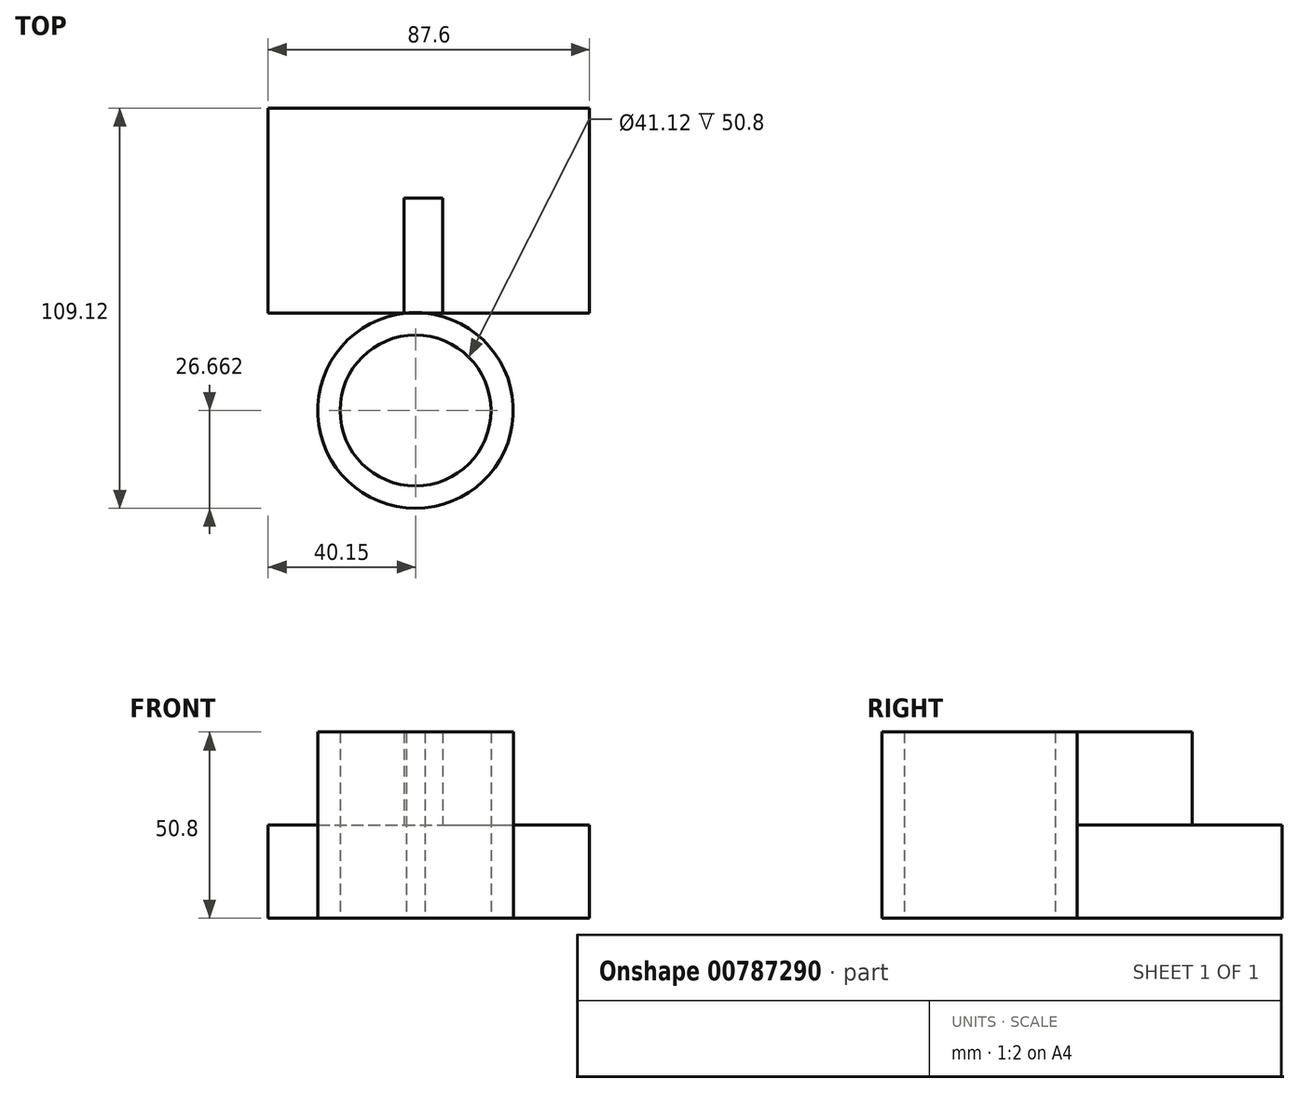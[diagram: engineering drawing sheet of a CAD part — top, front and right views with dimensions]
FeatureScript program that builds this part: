
annotation { "Feature Type Name" : "Feature", "Feature Type Description" : "" }
export const myFeature = defineFeature(function(context is Context, id is Id, definition is map)
    precondition{}
    {
        {
            var Q0;
            Q0=qCreatedBy(makeId("Top.planeOp"),FACE);
            var sketch = newSketch(context, id + "F0", { "sketchPlane" : qUnion([Q0])});
            skLineSegment(sketch, "E0.bottom", {"start": v(-40.15, 55.92) * mm, "end": v(47.45, 55.92) * mm});
            skLineSegment(sketch, "E0.top", {"start": v(-40.15, 0) * mm, "end": v(47.45, 0) * mm});
            skLineSegment(sketch, "E0.left", {"start": v(-40.15, 55.92) * mm, "end": v(-40.15, 0) * mm});
            skLineSegment(sketch, "E0.right", {"start": v(47.45, 55.92) * mm, "end": v(47.45, 0) * mm});
            skLineSegment(sketch, "E1.bottom", {"start": v(-3.07, 31.4) * mm, "end": v(7.45, 31.4) * mm});
            skLineSegment(sketch, "E1.top", {"start": v(-3.07, 0) * mm, "end": v(7.45, 0) * mm});
            skLineSegment(sketch, "E1.left", {"start": v(-3.07, 31.4) * mm, "end": v(-3.07, 0) * mm});
            skLineSegment(sketch, "E1.right", {"start": v(7.45, 31.4) * mm, "end": v(7.45, 0) * mm});
            skCircle(sketch, "E2", {"center": v(0, -26.54) * mm, "radius": 26.66 * mm});
            skCircle(sketch, "E3", {"center": v(0, -26.54) * mm, "radius": 20.56 * mm});
            skSolve(sketch);
        }
        {
            var Q0;
            Q0=makeQuery(id+"F0.imprint","IMPRINT",FACE,{"disambiguationData":[TD([[makeQuery(id+"F0.imprint","IMPRINT",EDGE,{"derivedFrom":sQuery(id+"F0.wireOp",EDGE,"E3")}),-1.0]])]});
            var Q1;
            Q1=makeQuery(id+"F0.imprint","IMPRINT",FACE,{"disambiguationData":[TD([[makeQuery(id+"F0.imprint","IMPRINT",EDGE,{"derivedFrom":sQuery(id+"F0.wireOp",EDGE,"E1.bottom")}),-1.0]])]});
            extrude(context, id + "F1", {"entities" : qUnion([Q0, Q1]), "depth" : 50.8 * mm, "offsetDistance" : 25.4 * mm});
        }
        {
            var Q0;
            Q0=makeQuery(id+"F0.imprint","IMPRINT",FACE,{"disambiguationData":[TD([[makeQuery(id+"F0.imprint","IMPRINT",EDGE,{"derivedFrom":sQuery(id+"F0.wireOp",EDGE,"E0.bottom")}),-1.0]])]});
            extrude(context, id + "F2", {"entities" : qUnion([Q0]), "operationType" : NewBodyOperationType.ADD, "depth" : 25.4 * mm, "offsetDistance" : 25.4 * mm});
        }
    });
